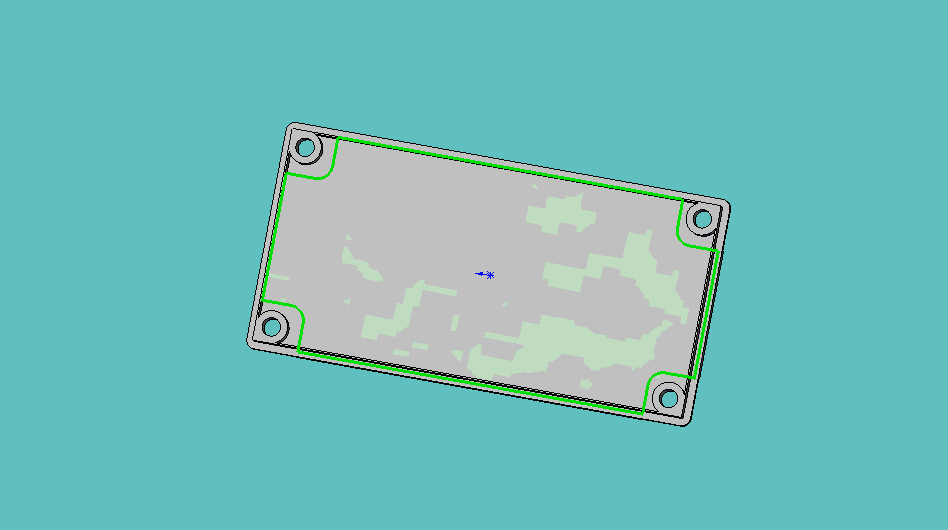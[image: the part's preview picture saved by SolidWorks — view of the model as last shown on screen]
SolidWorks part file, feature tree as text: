
SOLIDWORKS PART (.sldprt)
format: sldprt  version: not decoded by parser v0  size: 379,392 bytes
history: native  units: mm
features: sketch x3, extrude x2, mirror x2, material x1, fillet x1, cut_extrude x1 (+13 scaffold rows collapsed)
feature tree (23):
  scaffold x13  (default folders/planes/origin — collapsed)
  material  "ABS"
  sketch  "Sketch1"  dims[D1=~2.38125mm]
  extrude  "Extrude1"  Depth=1.5875mm
  fillet  "Fillet2"  Radius=0.508mm
  sketch  "Sketch2"  dims[D1=0.635mm]
  extrude  "Extrude2"  Depth=1.27mm
  sketch  "Sketch3"  dims[c1.D1=~1.841454mm c2.D1=45.0deg c2.D2=4.318mm]
  cut_extrude  "Cut-Extrude1"  Depth=0.508mm
  mirror  "Mirror1"
  mirror  "Mirror2"
decode coverage: 7 of 9 modeling features carry decoded parameters
note: ~ marks probable driven/reference dimensions
note: suppression state not decoded; provenance and decode notes live in map.json
